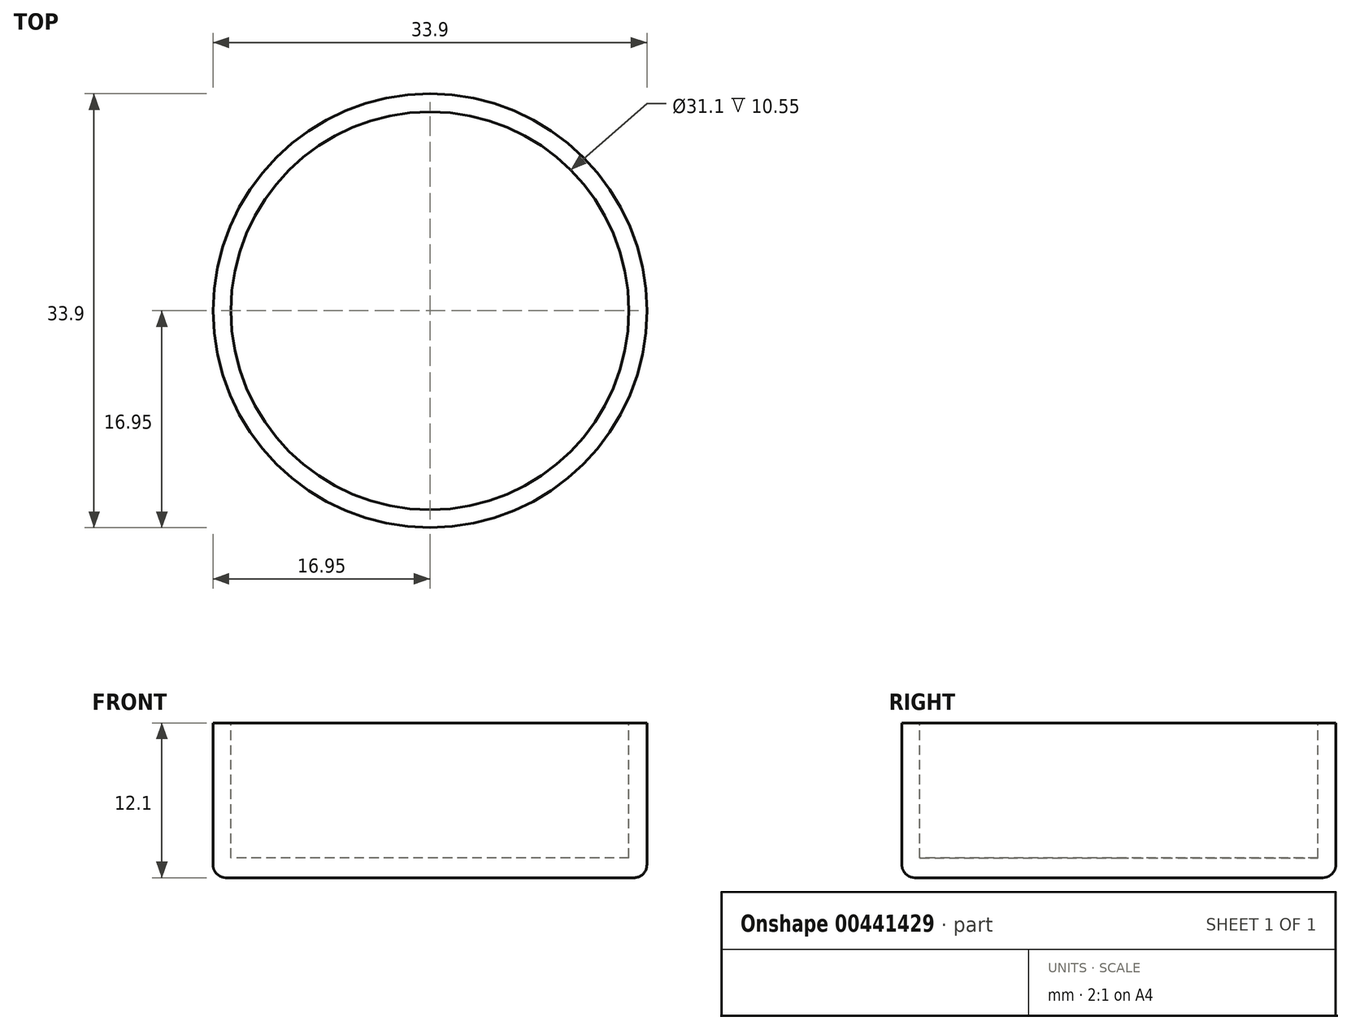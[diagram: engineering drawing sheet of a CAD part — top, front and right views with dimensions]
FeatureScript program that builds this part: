
annotation { "Feature Type Name" : "Feature", "Feature Type Description" : "" }
export const myFeature = defineFeature(function(context is Context, id is Id, definition is map)
    precondition{}
    {
        {
            var Q0;
            Q0=qCreatedBy(makeId("Top.planeOp"),FACE);
            var sketch = newSketch(context, id + "F0", { "sketchPlane" : qUnion([Q0])});
            skCircle(sketch, "E0", {"center": v(0, 0) * mm, "radius": 16.95 * mm});
            skSolve(sketch);
        }
        {
            var Q0;
            Q0=qSketchRegion(id+"F0",true);
            extrude(context, id + "F1", {"entities" : qUnion([Q0]), "depth" : 12.1 * mm});
        }
        {
            var Q0;
            Q0=makeQuery(id+"F1.opExtrude","CAP_FACE",FACE,{"disambiguationData":[OSD([sQuery(id+"F0.wireOp",EDGE,"E0")])],"isStart":false});
            var sketch = newSketch(context, id + "F2", { "sketchPlane" : qUnion([Q0])});
            skCircle(sketch, "E1", {"center": v(0, 0) * mm, "radius": 15.55 * mm});
            skSolve(sketch);
        }
        {
            var Q0;
            Q0=qSketchRegion(id+"F2",true);
            extrude(context, id + "F3", {"entities" : qUnion([Q0]), "operationType" : NewBodyOperationType.REMOVE, "oppositeDirection" : true, "depth" : 10.55 * mm});
        }
        {
            var Q0;
            Q0=makeQuery(id+"F1.opExtrude","CAP_EDGE",EDGE,{"disambiguationData":[OSD([sQuery(id+"F0.wireOp",EDGE,"E0")])],"isStart":true});
            fillet(context, id + "F4", {"entities" : qUnion([Q0]), "radius" : 1 * mm, "tangentPropagation" : true, "allowEdgeOverflow" : false});
        }
    });
